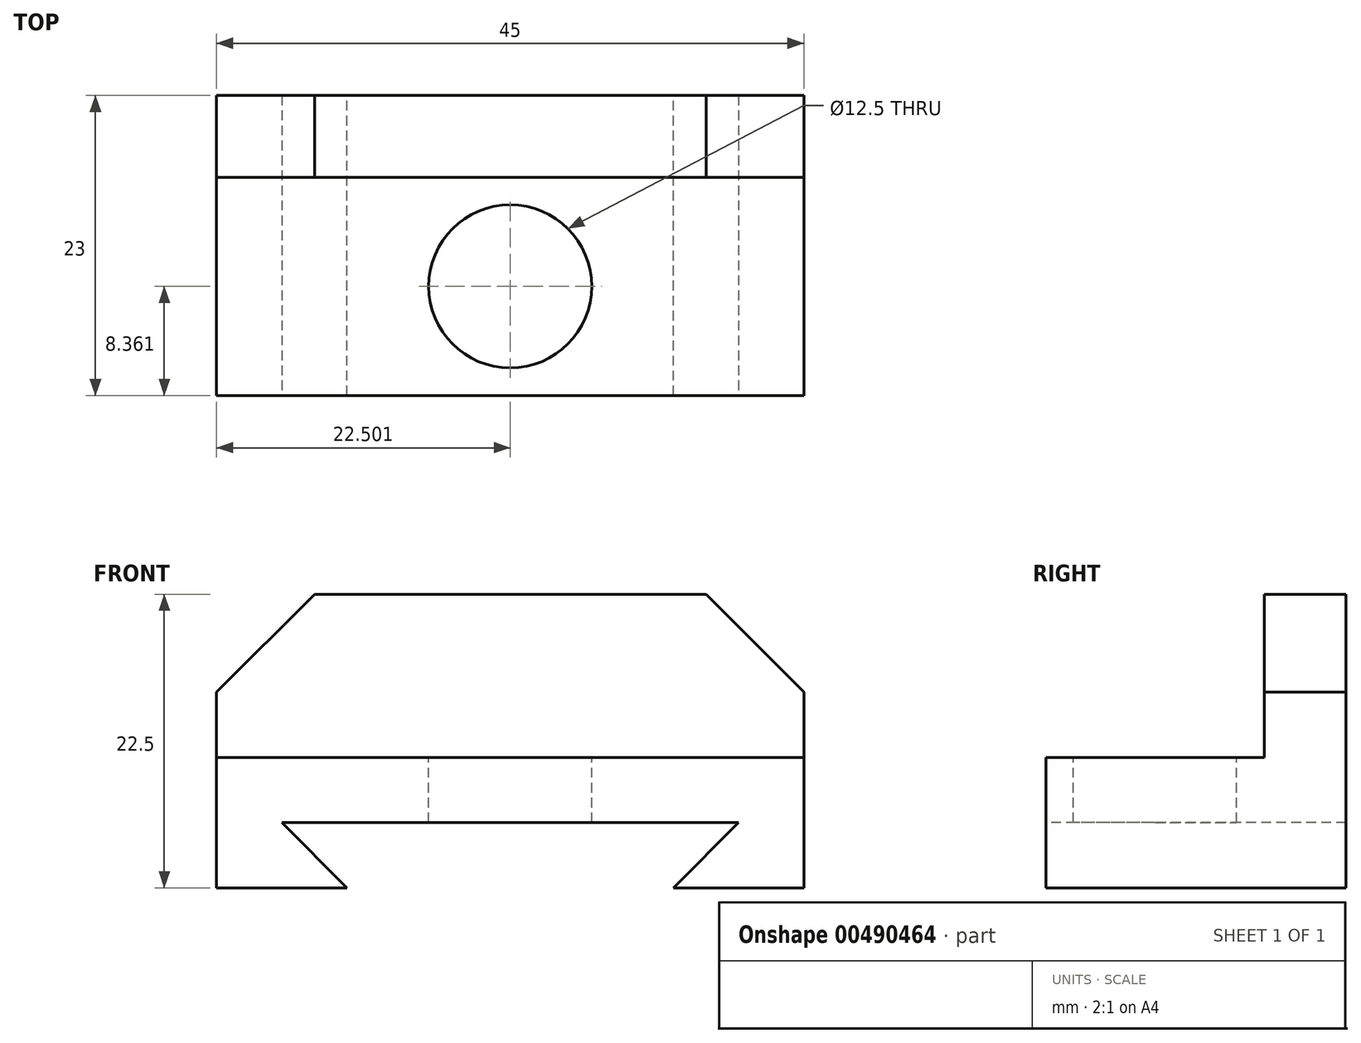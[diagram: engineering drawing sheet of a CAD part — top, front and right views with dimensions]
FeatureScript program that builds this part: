
annotation { "Feature Type Name" : "Feature", "Feature Type Description" : "" }
export const myFeature = defineFeature(function(context is Context, id is Id, definition is map)
    precondition{}
    {
        {
            var Q0;
            Q0=qCreatedBy(makeId("Front.planeOp"),FACE);
            var sketch = newSketch(context, id + "F0", { "sketchPlane" : qUnion([Q0])});
            skLineSegment(sketch, "E0.bottom", {"start": v(-20.67, -23.77) * mm, "end": v(24.33, -23.77) * mm});
            skLineSegment(sketch, "E0.top", {"start": v(-20.67, -33.77) * mm, "end": v(24.33, -33.77) * mm});
            skLineSegment(sketch, "E0.left", {"start": v(-20.67, -23.77) * mm, "end": v(-20.67, -33.77) * mm});
            skLineSegment(sketch, "E0.right", {"start": v(24.33, -23.77) * mm, "end": v(24.33, -33.77) * mm});
            skSolve(sketch);
        }
        {
            var Q0;
            Q0=makeQuery(id+"F0.imprint","IMPRINT",FACE,{"disambiguationData":[TD([[makeQuery(id+"F0.imprint","IMPRINT",EDGE,{"derivedFrom":sQuery(id+"F0.wireOp",EDGE,"E0.bottom")}),-1.0]])]});
            extrude(context, id + "F1", {"entities" : qUnion([Q0]), "depth" : 23 * mm});
        }
        {
            var Q0;
            Q0=makeQuery(id+"F1.opExtrude","SWEPT_FACE",FACE,{"disambiguationData":[OSD([sQuery(id+"F0.wireOp",EDGE,"E0.bottom")])]});
            var sketch = newSketch(context, id + "F2", { "sketchPlane" : qUnion([Q0])});
            skLineSegment(sketch, "E1", {"start": v(24.33, 0) * mm, "end": v(24.33, -6.28) * mm});
            skLineSegment(sketch, "E2", {"start": v(24.33, -6.28) * mm, "end": v(-20.67, -6.28) * mm});
            skLineSegment(sketch, "E3", {"start": v(-20.67, -6.28) * mm, "end": v(-20.67, 0) * mm});
            skLineSegment(sketch, "E4", {"start": v(-20.67, 0) * mm, "end": v(-13.17, 0) * mm});
            skLineSegment(sketch, "E5", {"start": v(-13.17, 0) * mm, "end": v(-13.17, -6.28) * mm});
            skLineSegment(sketch, "E6", {"start": v(24.33, 0) * mm, "end": v(16.83, 0) * mm});
            skLineSegment(sketch, "E7", {"start": v(-13.17, 0) * mm, "end": v(16.83, 0) * mm});
            skLineSegment(sketch, "E8", {"start": v(16.83, 0) * mm, "end": v(16.83, -6.28) * mm});
            skSolve(sketch);
        }
        {
            var Q0;
            {var subQ0=sQuery(id+"F2.wireOp",EDGE,"E5");Q0=makeQuery(id+"F2.imprint","IMPRINT",FACE,{"disambiguationData":[TD([[makeQuery(id+"F2.imprint","IMPRINT",EDGE,{"derivedFrom":subQ0}),1.0]])]});}
            var Q1;
            {var subQ0=sQuery(id+"F2.wireOp",EDGE,"E1");Q1=makeQuery(id+"F2.imprint","IMPRINT",FACE,{"disambiguationData":[TD([[makeQuery(id+"F2.imprint","IMPRINT",EDGE,{"derivedFrom":subQ0}),1.0]])]});}
            var Q2;
            {var subQ0=sQuery(id+"F2.wireOp",EDGE,"E3");Q2=makeQuery(id+"F2.imprint","IMPRINT",FACE,{"disambiguationData":[TD([[makeQuery(id+"F2.imprint","IMPRINT",EDGE,{"derivedFrom":subQ0}),-1.0]])]});}
            extrude(context, id + "F3", {"entities" : qUnion([Q0, Q1, Q2]), "operationType" : NewBodyOperationType.ADD, "depth" : 12.5 * mm});
        }
        {
            var Q0;
            Q0=makeQuery(id+"F3.opExtrude","SWEPT_FACE",FACE,{"disambiguationData":[OSD([sQuery(id+"F2.wireOp",EDGE,"E2")])]});
            var sketch = newSketch(context, id + "F4", { "sketchPlane" : qUnion([Q0])});
            skLineSegment(sketch, "E9", {"start": v(24.33, -23.77) * mm, "end": v(24.33, -18.77) * mm});
            skLineSegment(sketch, "E10", {"start": v(24.33, -11.27) * mm, "end": v(16.83, -11.27) * mm});
            skLineSegment(sketch, "E11", {"start": v(16.83, -11.27) * mm, "end": v(24.33, -18.77) * mm});
            skSolve(sketch);
        }
        {
            var Q0;
            {var subQ0=sQuery(id+"F4.wireOp",EDGE,"E10");Q0=makeQuery(id+"F4.imprint","IMPRINT",FACE,{"disambiguationData":[TD([[makeQuery(id+"F4.imprint","IMPRINT",EDGE,{"derivedFrom":subQ0}),1.0]])]});}
            extrude(context, id + "F5", {"entities" : qUnion([Q0]), "operationType" : NewBodyOperationType.REMOVE, "endBound" : BoundingType.THROUGH_ALL, "oppositeDirection" : true, "depth" : 25 * mm});
        }
        {
            var Q0;
            Q0=makeQuery(id+"F3.opExtrude","SWEPT_FACE",FACE,{"disambiguationData":[OSD([sQuery(id+"F2.wireOp",EDGE,"E2")])]});
            var sketch = newSketch(context, id + "F6", { "sketchPlane" : qUnion([Q0])});
            skLineSegment(sketch, "E12", {"start": v(-20.67, -23.77) * mm, "end": v(-20.67, -18.77) * mm});
            skLineSegment(sketch, "E13", {"start": v(-20.67, -11.27) * mm, "end": v(-13.17, -11.27) * mm});
            skLineSegment(sketch, "E14", {"start": v(-13.17, -11.27) * mm, "end": v(-20.67, -18.77) * mm});
            skSolve(sketch);
        }
        {
            var Q0;
            {var subQ0=sQuery(id+"F6.wireOp",EDGE,"E13");Q0=makeQuery(id+"F6.imprint","IMPRINT",FACE,{"disambiguationData":[TD([[makeQuery(id+"F6.imprint","IMPRINT",EDGE,{"derivedFrom":subQ0}),1.0]])]});}
            extrude(context, id + "F7", {"entities" : qUnion([Q0]), "operationType" : NewBodyOperationType.REMOVE, "endBound" : BoundingType.THROUGH_ALL, "oppositeDirection" : true, "depth" : 25 * mm});
        }
        {
            var Q0;
            Q0=makeQuery(id+"F1.opExtrude","SWEPT_FACE",FACE,{"disambiguationData":[OSD([sQuery(id+"F0.wireOp",EDGE,"E0.top")])]});
            var sketch = newSketch(context, id + "F8", { "sketchPlane" : qUnion([Q0])});
            skLineSegment(sketch, "E15", {"start": v(24.33, 23) * mm, "end": v(14.33, 23) * mm});
            skLineSegment(sketch, "E16", {"start": v(14.33, 23) * mm, "end": v(-10.67, 23) * mm});
            skLineSegment(sketch, "E17", {"start": v(-10.67, 23) * mm, "end": v(-10.67, 0) * mm});
            skLineSegment(sketch, "E18", {"start": v(14.33, 23) * mm, "end": v(14.33, 0) * mm});
            skSolve(sketch);
        }
        {
            var Q0;
            Q0=makeQuery(id+"F8.imprint","IMPRINT",FACE,{"disambiguationData":[TD([[makeQuery(id+"F8.imprint","IMPRINT",EDGE,{"derivedFrom":sQuery(id+"F8.wireOp",EDGE,"E16")}),-1.0]])]});
            extrude(context, id + "F9", {"entities" : qUnion([Q0]), "operationType" : NewBodyOperationType.REMOVE, "oppositeDirection" : true, "depth" : 5 * mm});
        }
        {
            var Q0;
            Q0=makeQuery(id+"F1.opExtrude","CAP_FACE",FACE,{"disambiguationData":[OSD([sQuery(id+"F0.wireOp",EDGE,"E0.bottom"),sQuery(id+"F0.wireOp",EDGE,"E0.top"),sQuery(id+"F0.wireOp",EDGE,"E0.left"),sQuery(id+"F0.wireOp",EDGE,"E0.right")])],"isStart":false});
            var sketch = newSketch(context, id + "F10", { "sketchPlane" : qUnion([Q0])});
            skLineSegment(sketch, "E19", {"start": v(14.33, -28.77) * mm, "end": v(19.33, -28.77) * mm});
            skLineSegment(sketch, "E20", {"start": v(19.33, -28.77) * mm, "end": v(14.33, -33.77) * mm});
            skLineSegment(sketch, "E21", {"start": v(-10.67, -28.77) * mm, "end": v(-15.67, -28.77) * mm});
            skLineSegment(sketch, "E22", {"start": v(-15.67, -28.77) * mm, "end": v(-10.67, -33.77) * mm});
            skSolve(sketch);
        }
        {
            var Q0;
            Q0=makeQuery(id+"F10.imprint","IMPRINT",FACE,{"disambiguationData":[TD([[makeQuery(id+"F10.imprint","IMPRINT",EDGE,{"derivedFrom":sQuery(id+"F10.wireOp",EDGE,"E21")}),1.0]])]});
            var Q1;
            Q1=makeQuery(id+"F10.imprint","IMPRINT",FACE,{"disambiguationData":[TD([[makeQuery(id+"F10.imprint","IMPRINT",EDGE,{"derivedFrom":sQuery(id+"F10.wireOp",EDGE,"E19")}),-1.0]])]});
            extrude(context, id + "F11", {"entities" : qUnion([Q0, Q1]), "operationType" : NewBodyOperationType.REMOVE, "endBound" : BoundingType.THROUGH_ALL, "oppositeDirection" : true, "depth" : 25 * mm});
        }
        {
            var Q0;
            Q0=makeQuery(id+"F1.opExtrude","SWEPT_FACE",FACE,{"disambiguationData":[OSD([sQuery(id+"F0.wireOp",EDGE,"E0.bottom")])]});
            var sketch = newSketch(context, id + "F12", { "sketchPlane" : qUnion([Q0])});
            skCircle(sketch, "E23", {"center": v(1.83, -14.64) * mm, "radius": 6.25 * mm});
            skPoint(sketch, "E23.centerSnap0", {"position": v(1.83, -23) * mm});
            skPoint(sketch, "E23.centerSnap1", {"position": v(-20.67, -14.64) * mm});
            skSolve(sketch);
        }
        {
            var Q0;
            Q0=makeQuery(id+"F12.imprint","IMPRINT",FACE,{"disambiguationData":[TD([[makeQuery(id+"F12.imprint","IMPRINT",EDGE,{"derivedFrom":sQuery(id+"F12.wireOp",EDGE,"E23")}),1.0]])]});
            extrude(context, id + "F13", {"entities" : qUnion([Q0]), "operationType" : NewBodyOperationType.REMOVE, "endBound" : BoundingType.THROUGH_ALL, "oppositeDirection" : true, "depth" : 25 * mm});
        }
    });
